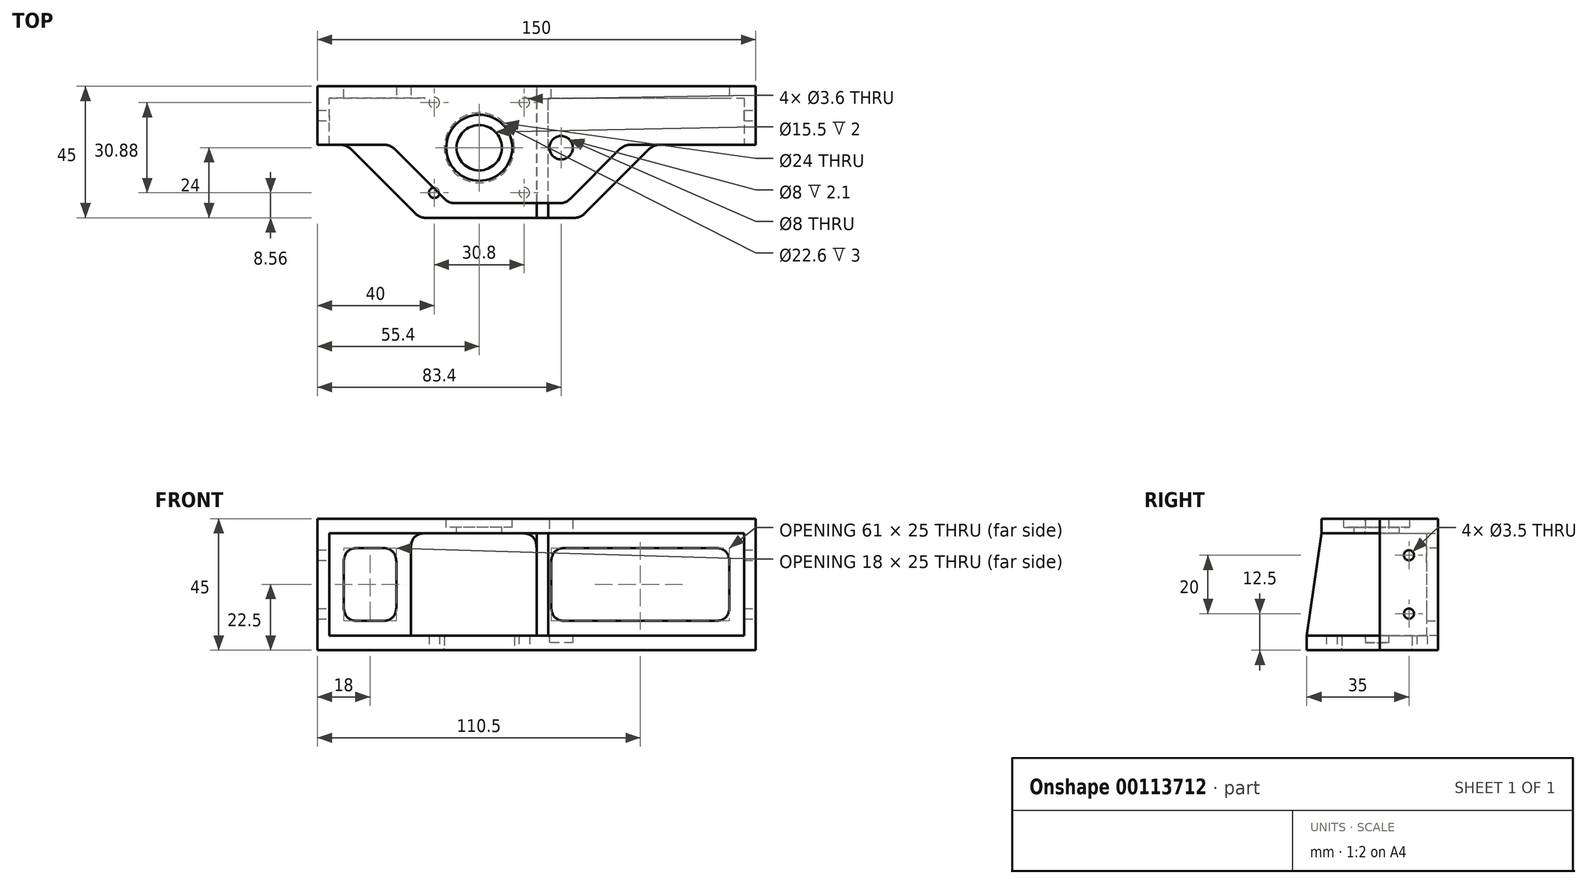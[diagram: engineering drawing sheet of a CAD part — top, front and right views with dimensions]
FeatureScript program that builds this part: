
annotation { "Feature Type Name" : "Feature", "Feature Type Description" : "" }
export const myFeature = defineFeature(function(context is Context, id is Id, definition is map)
    precondition{}
    {
        {
            var Q0;
            Q0=qCreatedBy(makeId("Top.planeOp"),FACE);
            var sketch = newSketch(context, id + "F0", { "sketchPlane" : qUnion([Q0])});
            skLineSegment(sketch, "E0.bottom", {"start": v(-75, 27) * mm, "end": v(75, 27) * mm});
            skLineSegment(sketch, "E0.top", {"start": v(-75, -27) * mm, "end": v(75, -27) * mm});
            skLineSegment(sketch, "E0.left", {"start": v(-75, 27) * mm, "end": v(-75, -27) * mm});
            skLineSegment(sketch, "E0.right", {"start": v(75, 27) * mm, "end": v(75, -27) * mm});
            skLineSegment(sketch, "E1", {"start": v(0, 27) * mm, "end": v(0, -27) * mm, "construction": true});
            skCircle(sketch, "E2", {"center": v(-35, 21.44) * mm, "radius": 1.8 * mm});
            skCircle(sketch, "E3.0.1.0", {"center": v(-35, -9.44) * mm, "radius": 1.8 * mm});
            skCircle(sketch, "E3.1.0.0", {"center": v(-4.2, 21.44) * mm, "radius": 1.8 * mm});
            skCircle(sketch, "E3.1.1.0", {"center": v(-4.2, -9.44) * mm, "radius": 1.8 * mm});
            skLineSegment(sketch, "E3.direction1", {"start": v(-35, 21.44) * mm, "end": v(-4.2, 21.44) * mm, "construction": true});
            skLineSegment(sketch, "E3.direction2", {"start": v(-35, 21.44) * mm, "end": v(-35, -9.44) * mm, "construction": true});
            skLineSegment(sketch, "E4", {"start": v(-19.6, 21.44) * mm, "end": v(-19.6, -9.44) * mm, "construction": true});
            skCircle(sketch, "E5", {"center": v(-19.6, 6) * mm, "radius": 12 * mm});
            skCircle(sketch, "E6", {"center": v(8.4, 6) * mm, "radius": 4 * mm});
            skLineSegment(sketch, "E7", {"start": v(-75, 7) * mm, "end": v(-65, 7) * mm});
            skLineSegment(sketch, "E8", {"start": v(-65, 7) * mm, "end": v(-40, -18) * mm});
            skLineSegment(sketch, "E9", {"start": v(-40, -18) * mm, "end": v(15, -18) * mm});
            skLineSegment(sketch, "E10", {"start": v(15, -18) * mm, "end": v(40, 7) * mm});
            skLineSegment(sketch, "E11", {"start": v(40, 7) * mm, "end": v(75, 7) * mm});
            skSolve(sketch);
        }
        {
            var Q0;
            {var subQ1=sQuery(id+"F0.wireOp",EDGE,"E0.bottom");Q0=makeQuery(id+"F0.imprint","IMPRINT",FACE,{"disambiguationData":[TD([[makeQuery(id+"F0.imprint","IMPRINT",EDGE,{"derivedFrom":subQ1}),-1.0]])]});}
            extrude(context, id + "F1", {"entities" : qUnion([Q0]), "depth" : 5 * mm});
        }
        {
            var Q0;
            Q0=makeQuery(id+"F1.opExtrude","CAP_FACE",FACE,{"disambiguationData":[OSD([sQuery(id+"F0.wireOp",EDGE,"E0.bottom"),sQuery(id+"F0.wireOp",EDGE,"E0.left"),sQuery(id+"F0.wireOp",EDGE,"E0.right"),sQuery(id+"F0.wireOp",EDGE,"E2"),sQuery(id+"F0.wireOp",EDGE,"E3.0.1.0"),sQuery(id+"F0.wireOp",EDGE,"E3.1.0.0"),sQuery(id+"F0.wireOp",EDGE,"E3.1.1.0"),sQuery(id+"F0.wireOp",EDGE,"E5"),sQuery(id+"F0.wireOp",EDGE,"E6"),sQuery(id+"F0.wireOp",EDGE,"E7"),sQuery(id+"F0.wireOp",EDGE,"E8"),sQuery(id+"F0.wireOp",EDGE,"E9"),sQuery(id+"F0.wireOp",EDGE,"E10"),sQuery(id+"F0.wireOp",EDGE,"E11")])],"isStart":false});
            var sketch = newSketch(context, id + "F2", { "sketchPlane" : qUnion([Q0])});
            skLineSegment(sketch, "E12.bottom", {"start": v(-75, 7) * mm, "end": v(-71, 7) * mm});
            skLineSegment(sketch, "E12.top", {"start": v(-75, 27) * mm, "end": v(-71, 27) * mm});
            skLineSegment(sketch, "E12.left", {"start": v(-75, 7) * mm, "end": v(-75, 27) * mm});
            skLineSegment(sketch, "E12.right", {"start": v(-71, 7) * mm, "end": v(-71, 27) * mm});
            skLineSegment(sketch, "E13.bottom", {"start": v(75, 27) * mm, "end": v(71, 27) * mm});
            skLineSegment(sketch, "E13.top", {"start": v(75, 7) * mm, "end": v(71, 7) * mm});
            skLineSegment(sketch, "E13.left", {"start": v(75, 27) * mm, "end": v(75, 7) * mm});
            skLineSegment(sketch, "E13.right", {"start": v(71, 27) * mm, "end": v(71, 7) * mm});
            skSolve(sketch);
        }
        {
            var Q0;
            Q0=makeQuery(id+"F2.imprint","IMPRINT",FACE,{"disambiguationData":[TD([[makeQuery(id+"F2.imprint","IMPRINT",EDGE,{"derivedFrom":sQuery(id+"F2.wireOp",EDGE,"E12.bottom")}),1.0]])]});
            var Q1;
            Q1=makeQuery(id+"F2.imprint","IMPRINT",FACE,{"disambiguationData":[TD([[makeQuery(id+"F2.imprint","IMPRINT",EDGE,{"derivedFrom":sQuery(id+"F2.wireOp",EDGE,"E13.bottom")}),-1.0]])]});
            extrude(context, id + "F3", {"entities" : qUnion([Q0, Q1]), "operationType" : NewBodyOperationType.ADD, "depth" : 40 * mm});
        }
        {
            var Q0;
            Q0=makeQuery(id+"F3.opExtrude","CAP_FACE",FACE,{"disambiguationData":[OSD([sQuery(id+"F2.wireOp",EDGE,"E13.bottom"),sQuery(id+"F2.wireOp",EDGE,"E13.top"),sQuery(id+"F2.wireOp",EDGE,"E13.left"),sQuery(id+"F2.wireOp",EDGE,"E13.right")])],"isStart":false});
            var sketch = newSketch(context, id + "F4", { "sketchPlane" : qUnion([Q0])});
            skLineSegment(sketch, "E14", {"start": v(75, 27) * mm, "end": v(-75, 27) * mm});
            skLineSegment(sketch, "E15", {"start": v(-75, 27) * mm, "end": v(-75, 7) * mm});
            skLineSegment(sketch, "E16", {"start": v(-75, 7) * mm, "end": v(-50, 7) * mm});
            skLineSegment(sketch, "E17", {"start": v(-50, 7) * mm, "end": v(-30, -13) * mm});
            skLineSegment(sketch, "E18", {"start": v(-30, -13) * mm, "end": v(10, -13) * mm});
            skLineSegment(sketch, "E19", {"start": v(10, -13) * mm, "end": v(30, 7) * mm});
            skLineSegment(sketch, "E20", {"start": v(30, 7) * mm, "end": v(75, 7) * mm});
            skLineSegment(sketch, "E21", {"start": v(75, 7) * mm, "end": v(75, 27) * mm});
            skCircle(sketch, "E22", {"center": v(-19.6, 6) * mm, "radius": 7.75 * mm});
            skCircle(sketch, "E23", {"center": v(-19.6, 6) * mm, "radius": 11.3 * mm});
            skCircle(sketch, "E24", {"center": v(-19.6, 6) * mm, "radius": 12.5 * mm});
            skSolve(sketch);
        }
        {
            var Q0;
            {var subQ1=sQuery(id+"F4.wireOp",EDGE,"E15");Q0=makeQuery(id+"F4.imprint","IMPRINT",FACE,{"disambiguationData":[TD([[makeQuery(id+"F4.imprint","IMPRINT",EDGE,{"derivedFrom":subQ1}),1.0]])]});}
            var Q1;
            Q1=makeQuery(id+"F4.imprint","IMPRINT",FACE,{"disambiguationData":[TD([[makeQuery(id+"F4.imprint","IMPRINT",EDGE,{"derivedFrom":sQuery(id+"F4.wireOp",EDGE,"E22")}),-1.0]])]});
            var Q2;
            Q2=makeQuery(id+"F4.imprint","IMPRINT",FACE,{"disambiguationData":[TD([[makeQuery(id+"F4.imprint","IMPRINT",EDGE,{"derivedFrom":sQuery(id+"F4.wireOp",EDGE,"E23")}),-1.0]])]});
            extrude(context, id + "F5", {"entities" : qUnion([Q0, Q1, Q2]), "operationType" : NewBodyOperationType.ADD, "oppositeDirection" : true, "depth" : 5 * mm});
        }
        {
            var Q0;
            Q0=makeQuery(id+"F0.imprint","IMPRINT",FACE,{"disambiguationData":[TD([[makeQuery(id+"F0.imprint","IMPRINT",EDGE,{"derivedFrom":sQuery(id+"F0.wireOp",EDGE,"E6")}),1.0]])]});
            extrude(context, id + "F6", {"entities" : qUnion([Q0]), "operationType" : NewBodyOperationType.REMOVE, "depth" : 50 * mm});
        }
        {
            var Q0;
            Q0=makeQuery(id+"F4.imprint","IMPRINT",FACE,{"disambiguationData":[TD([[makeQuery(id+"F4.imprint","IMPRINT",EDGE,{"derivedFrom":sQuery(id+"F4.wireOp",EDGE,"E22")}),-1.0]])]});
            extrude(context, id + "F7", {"entities" : qUnion([Q0]), "operationType" : NewBodyOperationType.REMOVE, "oppositeDirection" : true, "depth" : 3 * mm});
        }
        {
            var Q0;
            Q0=makeQuery(id+"F1.opExtrude","SWEPT_EDGE",EDGE,{"disambiguationData":[OSD([sQuery(id+"F0.wireOp",EDGE,"E7"),sQuery(id+"F0.wireOp",EDGE,"E8")])]});
            var Q1;
            Q1=makeQuery(id+"F1.opExtrude","SWEPT_EDGE",EDGE,{"disambiguationData":[OSD([sQuery(id+"F0.wireOp",EDGE,"E8"),sQuery(id+"F0.wireOp",EDGE,"E9")])]});
            var Q2;
            Q2=makeQuery(id+"F1.opExtrude","SWEPT_EDGE",EDGE,{"disambiguationData":[OSD([sQuery(id+"F0.wireOp",EDGE,"E10"),sQuery(id+"F0.wireOp",EDGE,"E11")])]});
            var Q3;
            Q3=makeQuery(id+"F1.opExtrude","SWEPT_EDGE",EDGE,{"disambiguationData":[OSD([sQuery(id+"F0.wireOp",EDGE,"E9"),sQuery(id+"F0.wireOp",EDGE,"E10")])]});
            var Q4;
            Q4=makeQuery(id+"F5.opExtrude","SWEPT_EDGE",EDGE,{"disambiguationData":[OSD([sQuery(id+"F4.wireOp",EDGE,"E16"),sQuery(id+"F4.wireOp",EDGE,"E17")])]});
            var Q5;
            Q5=makeQuery(id+"F5.opExtrude","SWEPT_EDGE",EDGE,{"disambiguationData":[OSD([sQuery(id+"F4.wireOp",EDGE,"E17"),sQuery(id+"F4.wireOp",EDGE,"E18")])]});
            var Q6;
            Q6=makeQuery(id+"F5.opExtrude","SWEPT_EDGE",EDGE,{"disambiguationData":[OSD([sQuery(id+"F4.wireOp",EDGE,"E18"),sQuery(id+"F4.wireOp",EDGE,"E19")])]});
            var Q7;
            Q7=makeQuery(id+"F5.opExtrude","SWEPT_EDGE",EDGE,{"disambiguationData":[OSD([sQuery(id+"F4.wireOp",EDGE,"E19"),sQuery(id+"F4.wireOp",EDGE,"E20")])]});
            fillet(context, id + "F8", {"entities" : qUnion([Q0, Q1, Q2, Q3, Q4, Q5, Q6, Q7]), "radius" : 5 * mm, "tangentPropagation" : true, "allowEdgeOverflow" : false});
        }
        {
            var Q0;
            Q0=makeQuery(id+"F1.opExtrude","CAP_EDGE",EDGE,{"disambiguationData":[OSD([sQuery(id+"F0.wireOp",EDGE,"E5")])],"isStart":false});
            var Q1;
            Q1=makeQuery(id+"F1.opExtrude","CAP_EDGE",EDGE,{"disambiguationData":[OSD([sQuery(id+"F0.wireOp",EDGE,"E5")])],"isStart":true});
            var Q2;
            Q2=makeQuery(id+"F1.opExtrude","CAP_EDGE",EDGE,{"disambiguationData":[OSD([sQuery(id+"F0.wireOp",EDGE,"E6")])],"isStart":false});
            var Q3;
            {var subQ0=sQuery(id+"F2.wireOp",EDGE,"E13.right");Q3=makeQuery(id+"F6.boolean.opBoolean","INTERSECT",EDGE,{"derivedFrom":[makeQuery(id+"F5.boolean.opBoolean","MERGE",FACE,{"derivedFrom":[makeQuery(id+"F3.opExtrude","CAP_FACE",FACE,{"disambiguationData":[OSD([sQuery(id+"F2.wireOp",EDGE,"E12.bottom"),sQuery(id+"F2.wireOp",EDGE,"E12.top"),sQuery(id+"F2.wireOp",EDGE,"E12.left"),sQuery(id+"F2.wireOp",EDGE,"E12.right")])],"isStart":false}),makeQuery(id+"F3.opExtrude","CAP_FACE",FACE,{"disambiguationData":[OSD([sQuery(id+"F2.wireOp",EDGE,"E13.bottom"),sQuery(id+"F2.wireOp",EDGE,"E13.top"),sQuery(id+"F2.wireOp",EDGE,"E13.left"),subQ0])],"isStart":false}),makeQuery(id+"F5.opExtrude","CAP_FACE",FACE,{"disambiguationData":[OSD([subQ0,sQuery(id+"F4.wireOp",EDGE,"E14"),sQuery(id+"F4.wireOp",EDGE,"E15"),sQuery(id+"F4.wireOp",EDGE,"E16"),sQuery(id+"F4.wireOp",EDGE,"E17"),sQuery(id+"F4.wireOp",EDGE,"E18"),sQuery(id+"F4.wireOp",EDGE,"E19"),sQuery(id+"F4.wireOp",EDGE,"E20"),sQuery(id+"F4.wireOp",EDGE,"E22")])],"isStart":true})]}),makeQuery(id+"F6.opExtrude","SWEPT_FACE",FACE,{"disambiguationData":[OSD([sQuery(id+"F0.wireOp",EDGE,"E6")])]})]});}
            var Q4;
            Q4=makeQuery(id+"F6.boolean.opBoolean","INTERSECT",EDGE,{"derivedFrom":[makeQuery(id+"F5.opExtrude","CAP_FACE",FACE,{"disambiguationData":[OSD([sQuery(id+"F2.wireOp",EDGE,"E13.right"),sQuery(id+"F4.wireOp",EDGE,"E14"),sQuery(id+"F4.wireOp",EDGE,"E15"),sQuery(id+"F4.wireOp",EDGE,"E16"),sQuery(id+"F4.wireOp",EDGE,"E17"),sQuery(id+"F4.wireOp",EDGE,"E18"),sQuery(id+"F4.wireOp",EDGE,"E19"),sQuery(id+"F4.wireOp",EDGE,"E20"),sQuery(id+"F4.wireOp",EDGE,"E22")])],"isStart":false}),makeQuery(id+"F6.opExtrude","SWEPT_FACE",FACE,{"disambiguationData":[OSD([sQuery(id+"F0.wireOp",EDGE,"E6")])]})]});
            fillet(context, id + "F9", {"entities" : qUnion([Q0, Q1, Q2, Q3, Q4]), "radius" : 0.4 * mm, "tangentPropagation" : true, "allowEdgeOverflow" : false});
        }
        {
            var Q0;
            Q0=makeQuery(id+"F0.imprint","IMPRINT",FACE,{"disambiguationData":[TD([[makeQuery(id+"F0.imprint","IMPRINT",EDGE,{"derivedFrom":sQuery(id+"F0.wireOp",EDGE,"E6")}),1.0]])]});
            extrude(context, id + "F10", {"entities" : qUnion([Q0]), "operationType" : NewBodyOperationType.ADD, "depth" : 2.5 * mm});
        }
        {
            var Q0;
            Q0=makeQuery(id+"F3.boolean.opBoolean","MERGE",FACE,{"derivedFrom":[makeQuery(id+"F1.opExtrude","SWEPT_FACE",FACE,{"disambiguationData":[OSD([sQuery(id+"F0.wireOp",EDGE,"E0.right")])]}),makeQuery(id+"F3.opExtrude","SWEPT_FACE",FACE,{"disambiguationData":[OSD([sQuery(id+"F2.wireOp",EDGE,"E13.left")])]})]});
            var sketch = newSketch(context, id + "F11", { "sketchPlane" : qUnion([Q0])});
            skCircle(sketch, "E25", {"center": v(17, 32.5) * mm, "radius": 1.75 * mm});
            skCircle(sketch, "E26", {"center": v(17, 12.5) * mm, "radius": 1.75 * mm});
            skLineSegment(sketch, "E27", {"start": v(17, 45) * mm, "end": v(17, 0) * mm, "construction": true});
            skSolve(sketch);
        }
        {
            var Q0;
            Q0=makeQuery(id+"F11.imprint","IMPRINT",FACE,{"disambiguationData":[TD([[makeQuery(id+"F11.imprint","IMPRINT",EDGE,{"derivedFrom":sQuery(id+"F11.wireOp",EDGE,"E25")}),1.0]])]});
            var Q1;
            Q1=makeQuery(id+"F11.imprint","IMPRINT",FACE,{"disambiguationData":[TD([[makeQuery(id+"F11.imprint","IMPRINT",EDGE,{"derivedFrom":sQuery(id+"F11.wireOp",EDGE,"E26")}),1.0]])]});
            extrude(context, id + "F12", {"entities" : qUnion([Q0, Q1]), "operationType" : NewBodyOperationType.REMOVE, "endBound" : BoundingType.THROUGH_ALL, "oppositeDirection" : true, "depth" : 100 * mm});
        }
        {
            var Q0;
            Q0=makeQuery(id+"F1.opExtrude","CAP_FACE",FACE,{"disambiguationData":[OSD([sQuery(id+"F0.wireOp",EDGE,"E0.bottom"),sQuery(id+"F0.wireOp",EDGE,"E0.left"),sQuery(id+"F0.wireOp",EDGE,"E0.right"),sQuery(id+"F0.wireOp",EDGE,"E2"),sQuery(id+"F0.wireOp",EDGE,"E3.0.1.0"),sQuery(id+"F0.wireOp",EDGE,"E3.1.0.0"),sQuery(id+"F0.wireOp",EDGE,"E3.1.1.0"),sQuery(id+"F0.wireOp",EDGE,"E5"),sQuery(id+"F0.wireOp",EDGE,"E6"),sQuery(id+"F0.wireOp",EDGE,"E7"),sQuery(id+"F0.wireOp",EDGE,"E8"),sQuery(id+"F0.wireOp",EDGE,"E9"),sQuery(id+"F0.wireOp",EDGE,"E10"),sQuery(id+"F0.wireOp",EDGE,"E11")])],"isStart":false});
            var sketch = newSketch(context, id + "F13", { "sketchPlane" : qUnion([Q0])});
            skLineSegment(sketch, "E28.bottom", {"start": v(-71, 27) * mm, "end": v(-43, 27) * mm});
            skLineSegment(sketch, "E28.top", {"start": v(-71, 23) * mm, "end": v(-43, 23) * mm});
            skLineSegment(sketch, "E28.left", {"start": v(-71, 27) * mm, "end": v(-71, 23) * mm});
            skLineSegment(sketch, "E28.right", {"start": v(-43, 27) * mm, "end": v(-43, 23) * mm});
            skLineSegment(sketch, "E29.bottom", {"start": v(71, 27) * mm, "end": v(0, 27) * mm});
            skLineSegment(sketch, "E29.top", {"start": v(71, 23) * mm, "end": v(0, 23) * mm});
            skLineSegment(sketch, "E29.left", {"start": v(71, 27) * mm, "end": v(71, 23) * mm});
            skLineSegment(sketch, "E29.right", {"start": v(0, 27) * mm, "end": v(0, 23) * mm});
            skSolve(sketch);
        }
        {
            var Q0;
            Q0=makeQuery(id+"F13.imprint","IMPRINT",FACE,{"disambiguationData":[TD([[makeQuery(id+"F13.imprint","IMPRINT",EDGE,{"derivedFrom":sQuery(id+"F13.wireOp",EDGE,"E28.bottom")}),-1.0]])]});
            var Q1;
            Q1=makeQuery(id+"F13.imprint","IMPRINT",FACE,{"disambiguationData":[TD([[makeQuery(id+"F13.imprint","IMPRINT",EDGE,{"derivedFrom":sQuery(id+"F13.wireOp",EDGE,"E29.bottom")}),-1.0]])]});
            extrude(context, id + "F14", {"entities" : qUnion([Q0, Q1]), "operationType" : NewBodyOperationType.ADD, "depth" : 40 * mm});
        }
        {
            var Q0;
            Q0=makeQuery(id+"F14.opExtrude","SWEPT_FACE",FACE,{"disambiguationData":[OSD([sQuery(id+"F13.wireOp",EDGE,"E28.top")])]});
            var sketch = newSketch(context, id + "F15", { "sketchPlane" : qUnion([Q0])});
            skLineSegment(sketch, "E30.bottom", {"start": v(-66, 35) * mm, "end": v(-48, 35) * mm});
            skLineSegment(sketch, "E30.top", {"start": v(-66, 10) * mm, "end": v(-48, 10) * mm});
            skLineSegment(sketch, "E30.left", {"start": v(-66, 35) * mm, "end": v(-66, 10) * mm});
            skLineSegment(sketch, "E30.right", {"start": v(-48, 35) * mm, "end": v(-48, 10) * mm});
            skLineSegment(sketch, "E31.bottom", {"start": v(5, 35) * mm, "end": v(66, 35) * mm});
            skLineSegment(sketch, "E31.top", {"start": v(5, 10) * mm, "end": v(66, 10) * mm});
            skLineSegment(sketch, "E31.left", {"start": v(5, 35) * mm, "end": v(5, 10) * mm});
            skLineSegment(sketch, "E31.right", {"start": v(66, 35) * mm, "end": v(66, 10) * mm});
            skSolve(sketch);
        }
        {
            var Q0;
            Q0=makeQuery(id+"F15.imprint","IMPRINT",FACE,{"disambiguationData":[TD([[makeQuery(id+"F15.imprint","IMPRINT",EDGE,{"derivedFrom":sQuery(id+"F15.wireOp",EDGE,"E30.bottom")}),-1.0]])]});
            var Q1;
            Q1=makeQuery(id+"F15.imprint","IMPRINT",FACE,{"disambiguationData":[TD([[makeQuery(id+"F15.imprint","IMPRINT",EDGE,{"derivedFrom":sQuery(id+"F15.wireOp",EDGE,"E31.bottom")}),-1.0]])]});
            extrude(context, id + "F16", {"entities" : qUnion([Q0, Q1]), "operationType" : NewBodyOperationType.REMOVE, "oppositeDirection" : true, "depth" : 25 * mm});
        }
        {
            var Q0;
            Q0=makeQuery(id+"F16.boolean.opBoolean","COPY",EDGE,{"derivedFrom":makeQuery(id+"F16.opExtrude","SWEPT_EDGE",EDGE,{"disambiguationData":[OSD([sQuery(id+"F15.wireOp",EDGE,"E30.bottom"),sQuery(id+"F15.wireOp",EDGE,"E30.left")])]})});
            var Q1;
            Q1=makeQuery(id+"F16.boolean.opBoolean","COPY",EDGE,{"derivedFrom":makeQuery(id+"F16.opExtrude","SWEPT_EDGE",EDGE,{"disambiguationData":[OSD([sQuery(id+"F15.wireOp",EDGE,"E31.bottom"),sQuery(id+"F15.wireOp",EDGE,"E31.left")])]})});
            var Q2;
            Q2=makeQuery(id+"F16.boolean.opBoolean","COPY",EDGE,{"derivedFrom":makeQuery(id+"F16.opExtrude","SWEPT_EDGE",EDGE,{"disambiguationData":[OSD([sQuery(id+"F15.wireOp",EDGE,"E30.top"),sQuery(id+"F15.wireOp",EDGE,"E30.right")])]})});
            var Q3;
            Q3=makeQuery(id+"F16.boolean.opBoolean","COPY",EDGE,{"derivedFrom":makeQuery(id+"F16.opExtrude","SWEPT_EDGE",EDGE,{"disambiguationData":[OSD([sQuery(id+"F15.wireOp",EDGE,"E31.top"),sQuery(id+"F15.wireOp",EDGE,"E31.right")])]})});
            var Q4;
            Q4=makeQuery(id+"F16.boolean.opBoolean","COPY",EDGE,{"derivedFrom":makeQuery(id+"F16.opExtrude","SWEPT_EDGE",EDGE,{"disambiguationData":[OSD([sQuery(id+"F15.wireOp",EDGE,"E31.bottom"),sQuery(id+"F15.wireOp",EDGE,"E31.right")])]})});
            var Q5;
            Q5=makeQuery(id+"F14.boolean.opBoolean","INTERSECT",EDGE,{"derivedFrom":[makeQuery(id+"F5.opExtrude","CAP_FACE",FACE,{"disambiguationData":[OSD([sQuery(id+"F2.wireOp",EDGE,"E13.right"),sQuery(id+"F4.wireOp",EDGE,"E14"),sQuery(id+"F4.wireOp",EDGE,"E15"),sQuery(id+"F4.wireOp",EDGE,"E16"),sQuery(id+"F4.wireOp",EDGE,"E17"),sQuery(id+"F4.wireOp",EDGE,"E18"),sQuery(id+"F4.wireOp",EDGE,"E19"),sQuery(id+"F4.wireOp",EDGE,"E20"),sQuery(id+"F4.wireOp",EDGE,"E22")])],"isStart":false}),makeQuery(id+"F14.opExtrude","SWEPT_FACE",FACE,{"disambiguationData":[OSD([sQuery(id+"F13.wireOp",EDGE,"E29.right")])]})]});
            var Q6;
            Q6=makeQuery(id+"F16.boolean.opBoolean","COPY",EDGE,{"derivedFrom":makeQuery(id+"F16.opExtrude","SWEPT_EDGE",EDGE,{"disambiguationData":[OSD([sQuery(id+"F15.wireOp",EDGE,"E30.bottom"),sQuery(id+"F15.wireOp",EDGE,"E30.right")])]})});
            var Q7;
            Q7=makeQuery(id+"F14.opExtrude","CAP_EDGE",EDGE,{"disambiguationData":[OSD([sQuery(id+"F13.wireOp",EDGE,"E28.right")])],"isStart":true});
            var Q8;
            Q8=makeQuery(id+"F16.boolean.opBoolean","COPY",EDGE,{"derivedFrom":makeQuery(id+"F16.opExtrude","SWEPT_EDGE",EDGE,{"disambiguationData":[OSD([sQuery(id+"F15.wireOp",EDGE,"E30.top"),sQuery(id+"F15.wireOp",EDGE,"E30.left")])]})});
            var Q9;
            Q9=makeQuery(id+"F16.boolean.opBoolean","COPY",EDGE,{"derivedFrom":makeQuery(id+"F16.opExtrude","SWEPT_EDGE",EDGE,{"disambiguationData":[OSD([sQuery(id+"F15.wireOp",EDGE,"E31.top"),sQuery(id+"F15.wireOp",EDGE,"E31.left")])]})});
            var Q10;
            Q10=makeQuery(id+"F14.boolean.opBoolean","INTERSECT",EDGE,{"derivedFrom":[makeQuery(id+"F5.opExtrude","CAP_FACE",FACE,{"disambiguationData":[OSD([sQuery(id+"F2.wireOp",EDGE,"E13.right"),sQuery(id+"F4.wireOp",EDGE,"E14"),sQuery(id+"F4.wireOp",EDGE,"E15"),sQuery(id+"F4.wireOp",EDGE,"E16"),sQuery(id+"F4.wireOp",EDGE,"E17"),sQuery(id+"F4.wireOp",EDGE,"E18"),sQuery(id+"F4.wireOp",EDGE,"E19"),sQuery(id+"F4.wireOp",EDGE,"E20"),sQuery(id+"F4.wireOp",EDGE,"E22")])],"isStart":false}),makeQuery(id+"F14.opExtrude","SWEPT_FACE",FACE,{"disambiguationData":[OSD([sQuery(id+"F13.wireOp",EDGE,"E28.right")])]})]});
            fillet(context, id + "F17", {"entities" : qUnion([Q0, Q1, Q2, Q3, Q4, Q5, Q6, Q7, Q8, Q9, Q10]), "radius" : 5 * mm, "tangentPropagation" : true, "rho" : 0.5, "crossSection" : FilletCrossSection.CONIC, "allowEdgeOverflow" : false});
        }
        {
            var Q0;
            Q0=makeQuery(id+"F14.opExtrude","SWEPT_FACE",FACE,{"disambiguationData":[OSD([sQuery(id+"F13.wireOp",EDGE,"E29.top")])]});
            var sketch = newSketch(context, id + "F18", { "sketchPlane" : qUnion([Q0])});
            skLineSegment(sketch, "E32.left", {"start": v(0, 5) * mm, "end": v(0, 40.1) * mm});
            skLineSegment(sketch, "E33", {"start": v(0, 40.1) * mm, "end": v(4, 40) * mm});
            skLineSegment(sketch, "E34", {"start": v(4, 40) * mm, "end": v(4, 5) * mm});
            skLineSegment(sketch, "E35", {"start": v(4, 5) * mm, "end": v(0, 5) * mm});
            skSolve(sketch);
        }
        {
            var Q0;
            {var subQ0=sQuery(id+"F18.wireOp",EDGE,"E34");Q0=makeQuery(id+"F18.imprint","IMPRINT",FACE,{"disambiguationData":[TD([[makeQuery(id+"F18.imprint","IMPRINT",EDGE,{"derivedFrom":subQ0}),-1.0]])]});}
            extrude(context, id + "F19", {"entities" : qUnion([Q0]), "operationType" : NewBodyOperationType.ADD, "depth" : 41 * mm});
        }
        {
            var Q0;
            Q0=makeQuery(id+"F19.opExtrude","SWEPT_FACE",FACE,{"disambiguationData":[OSD([sQuery(id+"F18.wireOp",EDGE,"E34")])]});
            var sketch = newSketch(context, id + "F20", { "sketchPlane" : qUnion([Q0])});
            skLineSegment(sketch, "E36", {"start": v(-13, 40) * mm, "end": v(-18, 5) * mm});
            skLineSegment(sketch, "E37", {"start": v(-18, 5) * mm, "end": v(-18, 40) * mm});
            skLineSegment(sketch, "E38", {"start": v(-18, 40) * mm, "end": v(-13, 40) * mm});
            skSolve(sketch);
        }
        {
            var Q0;
            Q0=makeQuery(id+"F20.imprint","IMPRINT",FACE,{"disambiguationData":[TD([[makeQuery(id+"F20.imprint","IMPRINT",EDGE,{"derivedFrom":sQuery(id+"F20.wireOp",EDGE,"E36")}),-1.0]])]});
            extrude(context, id + "F21", {"entities" : qUnion([Q0]), "operationType" : NewBodyOperationType.REMOVE, "oppositeDirection" : true, "depth" : 5 * mm});
        }
    });
